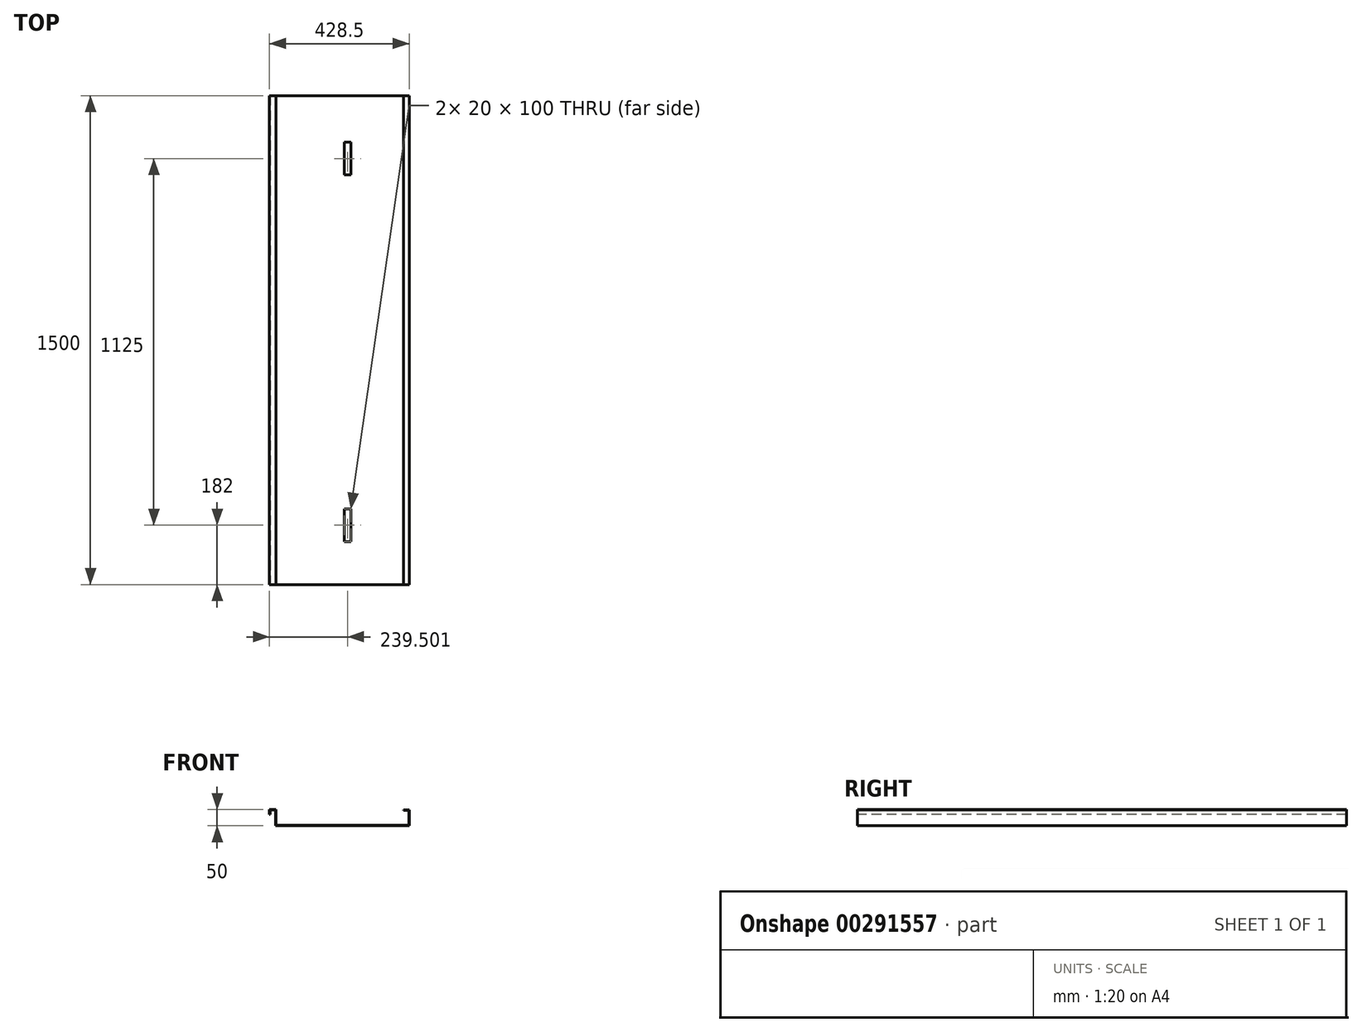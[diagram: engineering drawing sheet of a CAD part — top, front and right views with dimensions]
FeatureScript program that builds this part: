
annotation { "Feature Type Name" : "Feature", "Feature Type Description" : "" }
export const myFeature = defineFeature(function(context is Context, id is Id, definition is map)
    precondition{}
    {
        {
            var Q0;
            Q0=qCreatedBy(makeId("Front.planeOp"),FACE);
            var sketch = newSketch(context, id + "F0", { "sketchPlane" : qUnion([Q0])});
            skLineSegment(sketch, "E0", {"start": v(9.56, 16.63) * mm, "end": v(419.56, 16.63) * mm});
            skLineSegment(sketch, "E1", {"start": v(419.56, 16.63) * mm, "end": v(419.56, 65.13) * mm});
            skLineSegment(sketch, "E2", {"start": v(419.56, 65.13) * mm, "end": v(402.56, 65.13) * mm});
            skLineSegment(sketch, "E3", {"start": v(402.56, 65.13) * mm, "end": v(402.56, 63.63) * mm});
            skLineSegment(sketch, "E4", {"start": v(402.56, 63.63) * mm, "end": v(418.06, 63.63) * mm});
            skLineSegment(sketch, "E5", {"start": v(9.56, 16.63) * mm, "end": v(9.56, 65.13) * mm});
            skLineSegment(sketch, "E6", {"start": v(418.06, 63.63) * mm, "end": v(418.06, 18.13) * mm});
            skLineSegment(sketch, "E7", {"start": v(418.06, 18.13) * mm, "end": v(11.06, 18.13) * mm});
            skLineSegment(sketch, "E8", {"start": v(11.06, 18.13) * mm, "end": v(11.06, 66.63) * mm});
            skLineSegment(sketch, "E9", {"start": v(11.06, 66.63) * mm, "end": v(-8.94, 66.63) * mm});
            skLineSegment(sketch, "E10", {"start": v(-8.94, 66.63) * mm, "end": v(-8.94, 51.63) * mm});
            skLineSegment(sketch, "E11", {"start": v(-8.94, 51.63) * mm, "end": v(-7.44, 51.63) * mm});
            skLineSegment(sketch, "E12", {"start": v(-7.44, 51.63) * mm, "end": v(-7.44, 65.13) * mm});
            skLineSegment(sketch, "E13", {"start": v(-7.44, 65.13) * mm, "end": v(9.56, 65.13) * mm});
            skSolve(sketch);
        }
        {
            var Q0;
            Q0=makeQuery(id+"F0.imprint","IMPRINT",FACE,{"disambiguationData":[TD([[makeQuery(id+"F0.imprint","IMPRINT",EDGE,{"derivedFrom":sQuery(id+"F0.wireOp",EDGE,"E0")}),1.0]])]});
            extrude(context, id + "F1", {"entities" : qUnion([Q0]), "oppositeDirection" : true, "depth" : 1500 * mm});
        }
        {
            var Q0;
            Q0=makeQuery(id+"F1.opExtrude","SWEPT_FACE",FACE,{"disambiguationData":[OSD([sQuery(id+"F0.wireOp",EDGE,"E7")])]});
            var sketch = newSketch(context, id + "F2", { "sketchPlane" : qUnion([Q0])});
            skPoint(sketch, "E14.startSnap0", {"position": v(214.56, 0) * mm});
            skLineSegment(sketch, "E15.bottom", {"start": v(220.56, 232) * mm, "end": v(240.56, 232) * mm});
            skLineSegment(sketch, "E15.top", {"start": v(220.56, 132) * mm, "end": v(240.56, 132) * mm});
            skLineSegment(sketch, "E15.left", {"start": v(220.56, 232) * mm, "end": v(220.56, 132) * mm});
            skLineSegment(sketch, "E15.right", {"start": v(240.56, 232) * mm, "end": v(240.56, 132) * mm});
            skPoint(sketch, "E15.middle", {"position": v(230.56, 182) * mm});
            skLineSegment(sketch, "E16", {"start": v(230.56, 182) * mm, "end": v(230.56, 1357) * mm, "construction": true});
            skLineSegment(sketch, "E17", {"start": v(240.56, 1357) * mm, "end": v(220.56, 1357) * mm});
            skLineSegment(sketch, "E18", {"start": v(220.56, 1357) * mm, "end": v(220.56, 1257) * mm});
            skLineSegment(sketch, "E19", {"start": v(220.56, 1257) * mm, "end": v(240.56, 1257) * mm});
            skLineSegment(sketch, "E20", {"start": v(240.56, 1257) * mm, "end": v(240.56, 1357) * mm});
            skSolve(sketch);
        }
        {
            var Q0;
            Q0=makeQuery(id+"F2.imprint","IMPRINT",FACE,{"disambiguationData":[TD([[makeQuery(id+"F2.imprint","IMPRINT",EDGE,{"derivedFrom":sQuery(id+"F2.wireOp",EDGE,"E15.bottom")}),-1.0]])]});
            var Q1;
            Q1=makeQuery(id+"F2.imprint","IMPRINT",FACE,{"disambiguationData":[TD([[makeQuery(id+"F2.imprint","IMPRINT",EDGE,{"derivedFrom":sQuery(id+"F2.wireOp",EDGE,"E17")}),1.0]])]});
            extrude(context, id + "F3", {"entities" : qUnion([Q0, Q1]), "operationType" : NewBodyOperationType.REMOVE, "endBound" : BoundingType.UP_TO_NEXT, "oppositeDirection" : true, "depth" : 25 * mm});
        }
    });
